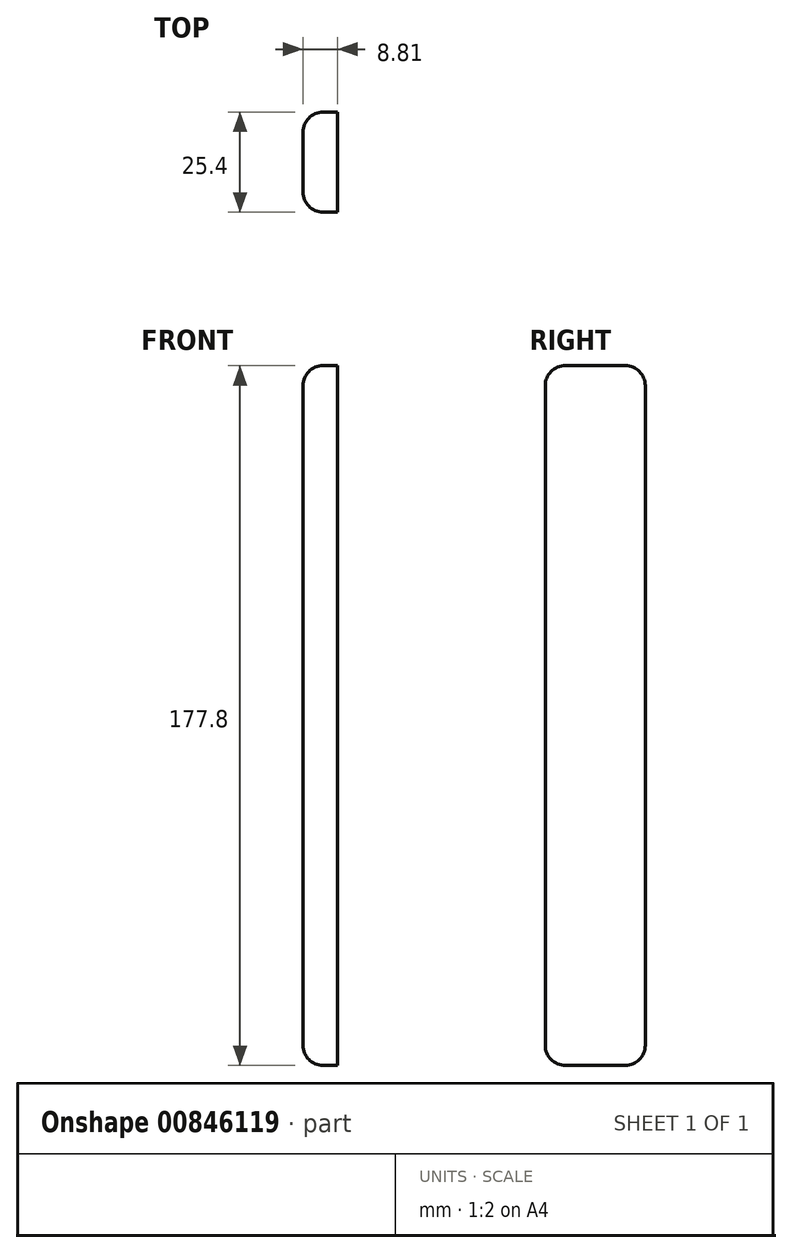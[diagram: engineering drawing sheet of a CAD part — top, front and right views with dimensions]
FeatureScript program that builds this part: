
annotation { "Feature Type Name" : "Feature", "Feature Type Description" : "" }
export const myFeature = defineFeature(function(context is Context, id is Id, definition is map)
    precondition{}
    {
        {
            var Q0;
            Q0=qCreatedBy(makeId("Top.planeOp"),FACE);
            var sketch = newSketch(context, id + "F0", { "sketchPlane" : qUnion([Q0])});
            skLineSegment(sketch, "E0.bottom", {"start": v(-42.57, 29.75) * mm, "end": v(-33.76, 29.75) * mm});
            skLineSegment(sketch, "E0.top", {"start": v(-42.57, 4.35) * mm, "end": v(-33.76, 4.35) * mm});
            skLineSegment(sketch, "E0.left", {"start": v(-42.57, 29.75) * mm, "end": v(-42.57, 4.35) * mm});
            skLineSegment(sketch, "E0.right", {"start": v(-33.76, 29.75) * mm, "end": v(-33.76, 4.35) * mm});
            skSolve(sketch);
        }
        {
            var Q0;
            Q0 = qSketchRegion(id + "F0", true);
            extrude(context, id + "F1", {"entities" : qUnion([Q0]), "depth" : 88.9 * mm, "offsetDistance" : 25.4 * mm, "hasSecondDirection" : true, "secondDirectionOppositeDirection" : true, "secondDirectionDepth" : 88.9 * mm});
        }
        {
            var Q0;
            Q0=makeQuery(id+"F1.opExtrude","SWEPT_EDGE",EDGE,{"disambiguationData":[OSD([sQuery(id+"F0.wireOp",EDGE,"E0.top"),sQuery(id+"F0.wireOp",EDGE,"E0.left")])]});
            fillet(context, id + "F2", {"entities" : qUnion([Q0]), "radius" : 5.08 * mm, "tangentPropagation" : true, "allowEdgeOverflow" : false});
        }
        {
            var Q0;
            Q0=makeQuery(id+"F1.opExtrude","SWEPT_EDGE",EDGE,{"disambiguationData":[OSD([sQuery(id+"F0.wireOp",EDGE,"E0.bottom"),sQuery(id+"F0.wireOp",EDGE,"E0.left")])]});
            fillet(context, id + "F3", {"entities" : qUnion([Q0]), "radius" : 5.08 * mm, "tangentPropagation" : true, "allowEdgeOverflow" : false});
        }
        {
            var Q0;
            Q0=makeQuery(id+"F1.opExtrude","CAP_EDGE",EDGE,{"disambiguationData":[OSD([sQuery(id+"F0.wireOp",EDGE,"E0.left")])],"isStart":false});
            fillet(context, id + "F4", {"entities" : qUnion([Q0]), "radius" : 5.08 * mm, "tangentPropagation" : true, "allowEdgeOverflow" : false});
        }
        {
            var Q0;
            Q0=makeQuery(id+"F1.opExtrude","CAP_EDGE",EDGE,{"disambiguationData":[OSD([sQuery(id+"F0.wireOp",EDGE,"E0.left")])],"isStart":true});
            fillet(context, id + "F5", {"entities" : qUnion([Q0]), "radius" : 5.08 * mm, "tangentPropagation" : true, "allowEdgeOverflow" : false});
        }
    });
